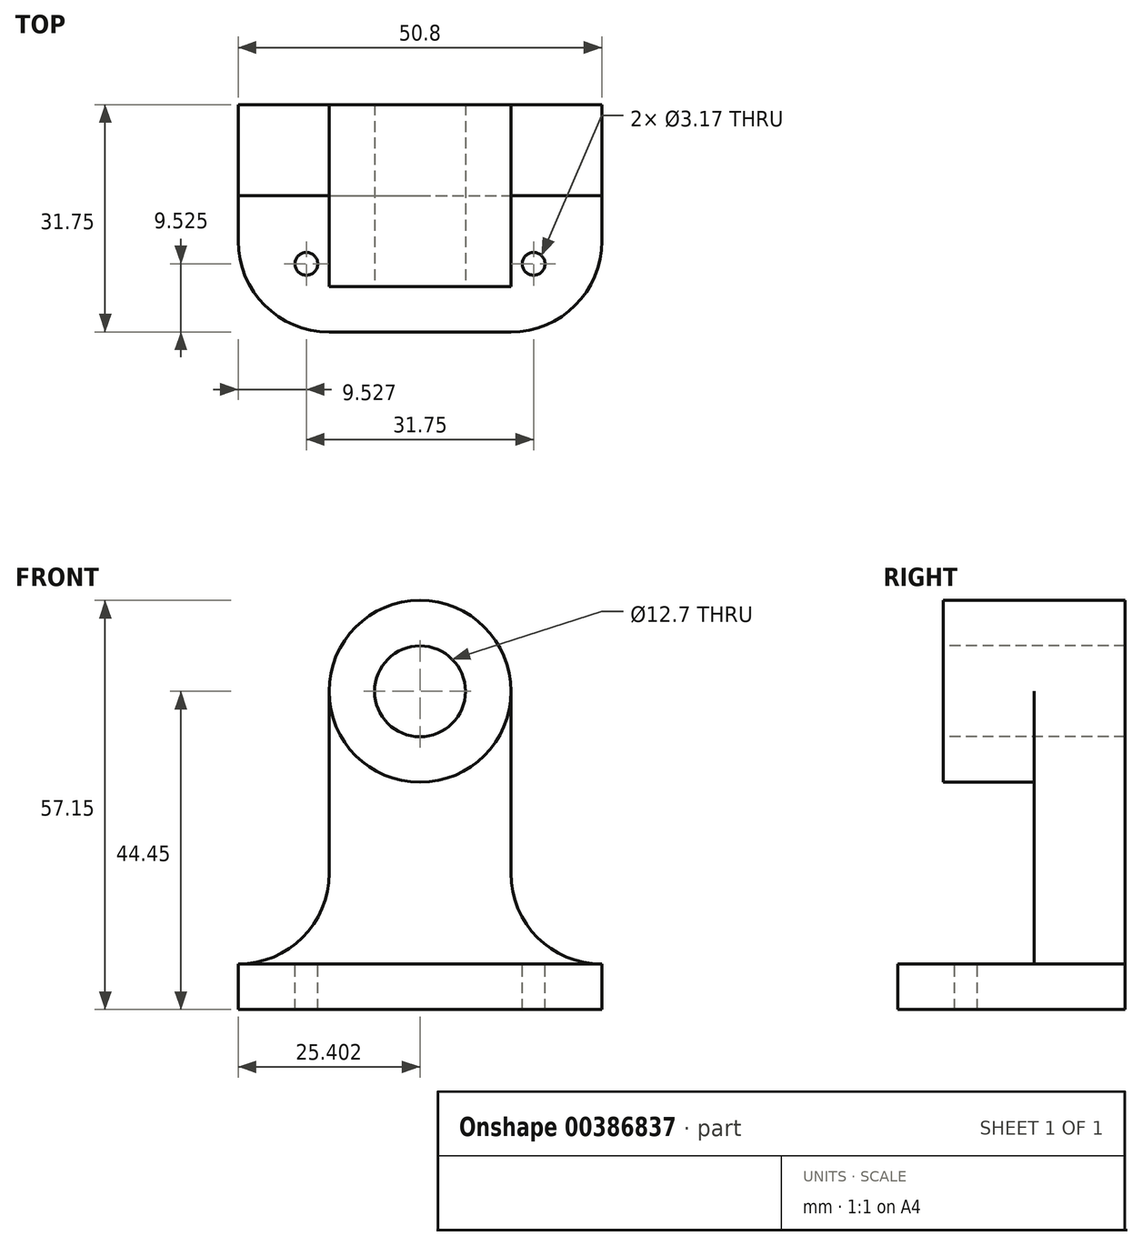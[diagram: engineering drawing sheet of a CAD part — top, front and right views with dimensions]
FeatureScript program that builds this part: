
annotation { "Feature Type Name" : "Feature", "Feature Type Description" : "" }
export const myFeature = defineFeature(function(context is Context, id is Id, definition is map)
    precondition{}
    {
        {
            var Q0;
            Q0=qCreatedBy(makeId("Front.planeOp"),FACE);
            var sketch = newSketch(context, id + "F0", { "sketchPlane" : qUnion([Q0])});
            skLineSegment(sketch, "E0", {"start": v(-22.4, 6.35) * mm, "end": v(-22.4, 0) * mm});
            skLineSegment(sketch, "E1", {"start": v(-22.4, 0) * mm, "end": v(28.4, 0) * mm});
            skLineSegment(sketch, "E2", {"start": v(28.4, 0) * mm, "end": v(28.4, 6.35) * mm});
            skLineSegment(sketch, "E3", {"start": v(28.4, 6.35) * mm, "end": v(15.7, 6.35) * mm});
            skLineSegment(sketch, "E4", {"start": v(-22.4, 6.35) * mm, "end": v(-9.7, 6.35) * mm});
            skLineSegment(sketch, "E5", {"start": v(-9.7, 6.35) * mm, "end": v(-9.7, 57.15) * mm});
            skLineSegment(sketch, "E6", {"start": v(15.7, 6.35) * mm, "end": v(15.7, 57.15) * mm});
            skLineSegment(sketch, "E7", {"start": v(15.7, 57.15) * mm, "end": v(-9.7, 57.15) * mm});
            skSolve(sketch);
        }
        {
            var Q0;
            Q0=makeQuery(id+"F0.imprint","IMPRINT",FACE,{"disambiguationData":[TD([[makeQuery(id+"F0.imprint","IMPRINT",EDGE,{"derivedFrom":sQuery(id+"F0.wireOp",EDGE,"E0")}),1.0]])]});
            extrude(context, id + "F1", {"entities" : qUnion([Q0]), "depth" : 31.75 * mm});
        }
        {
            var Q0;
            Q0=makeQuery(id+"F1.opExtrude","CAP_FACE",FACE,{"disambiguationData":[OSD([sQuery(id+"F0.wireOp",EDGE,"E0"),sQuery(id+"F0.wireOp",EDGE,"E1"),sQuery(id+"F0.wireOp",EDGE,"E2"),sQuery(id+"F0.wireOp",EDGE,"E3"),sQuery(id+"F0.wireOp",EDGE,"E4"),sQuery(id+"F0.wireOp",EDGE,"E5"),sQuery(id+"F0.wireOp",EDGE,"E6"),sQuery(id+"F0.wireOp",EDGE,"E7")])],"isStart":false});
            var sketch = newSketch(context, id + "F2", { "sketchPlane" : qUnion([Q0])});
            skCircle(sketch, "E8", {"center": v(3, 44.45) * mm, "radius": 6.35 * mm});
            skSolve(sketch);
        }
        {
            var Q0;
            Q0=makeQuery(id+"F2.imprint","IMPRINT",FACE,{"disambiguationData":[TD([[makeQuery(id+"F2.imprint","IMPRINT",EDGE,{"derivedFrom":sQuery(id+"F2.wireOp",EDGE,"E8")}),1.0]])]});
            extrude(context, id + "F3", {"entities" : qUnion([Q0]), "operationType" : NewBodyOperationType.REMOVE, "oppositeDirection" : true, "depth" : 31.75 * mm});
        }
        {
            var Q0;
            Q0=makeQuery(id+"F1.opExtrude","CAP_FACE",FACE,{"disambiguationData":[OSD([sQuery(id+"F0.wireOp",EDGE,"E0"),sQuery(id+"F0.wireOp",EDGE,"E1"),sQuery(id+"F0.wireOp",EDGE,"E2"),sQuery(id+"F0.wireOp",EDGE,"E3"),sQuery(id+"F0.wireOp",EDGE,"E4"),sQuery(id+"F0.wireOp",EDGE,"E5"),sQuery(id+"F0.wireOp",EDGE,"E6"),sQuery(id+"F0.wireOp",EDGE,"E7")])],"isStart":false});
            var sketch = newSketch(context, id + "F4", { "sketchPlane" : qUnion([Q0])});
            skCircle(sketch, "E9", {"center": v(3, 44.45) * mm, "radius": 12.7 * mm});
            skSolve(sketch);
        }
        {
            var Q0;
            {var subQ0=sQuery(id+"F4.wireOp",EDGE,"E9");var subQ1=makeQuery(id+"F1.opExtrude","CAP_EDGE",EDGE,{"disambiguationData":[OSD([sQuery(id+"F0.wireOp",EDGE,"E7")])],"isStart":false});var subQ2=makeQuery(id+"F4.imprint","INTERSECT",VERTEX,{"derivedFrom":[subQ1,subQ0]});Q0=makeQuery(id+"F4.imprint","IMPRINT",FACE,{"disambiguationData":[TD([[makeQuery(id+"F4.imprint","IMPRINT",EDGE,{"disambiguationData":[TD([[subQ2,-1.0]])],"derivedFrom":subQ0}),-1.0]])]});}
            var Q1;
            {var subQ0=sQuery(id+"F4.wireOp",EDGE,"E9");var subQ1=makeQuery(id+"F1.opExtrude","CAP_EDGE",EDGE,{"disambiguationData":[OSD([sQuery(id+"F0.wireOp",EDGE,"E7")])],"isStart":false});var subQ2=makeQuery(id+"F4.imprint","INTERSECT",VERTEX,{"derivedFrom":[subQ1,subQ0]});Q1=makeQuery(id+"F4.imprint","IMPRINT",FACE,{"disambiguationData":[TD([[makeQuery(id+"F4.imprint","IMPRINT",EDGE,{"disambiguationData":[TD([[subQ2,1.0]])],"derivedFrom":subQ0}),-1.0]])]});}
            extrude(context, id + "F5", {"entities" : qUnion([Q0, Q1]), "operationType" : NewBodyOperationType.REMOVE, "oppositeDirection" : true, "depth" : 31.75 * mm});
        }
        {
            var Q0;
            Q0=makeQuery(id+"F1.opExtrude","CAP_FACE",FACE,{"disambiguationData":[OSD([sQuery(id+"F0.wireOp",EDGE,"E0"),sQuery(id+"F0.wireOp",EDGE,"E1"),sQuery(id+"F0.wireOp",EDGE,"E2"),sQuery(id+"F0.wireOp",EDGE,"E3"),sQuery(id+"F0.wireOp",EDGE,"E4"),sQuery(id+"F0.wireOp",EDGE,"E5"),sQuery(id+"F0.wireOp",EDGE,"E6"),sQuery(id+"F0.wireOp",EDGE,"E7")])],"isStart":false});
            var sketch = newSketch(context, id + "F6", { "sketchPlane" : qUnion([Q0])});
            skCircle(sketch, "E10", {"center": v(3, 44.45) * mm, "radius": 12.7 * mm});
            skLineSegment(sketch, "E11", {"start": v(-9.7, 6.35) * mm, "end": v(15.7, 6.35) * mm});
            skSolve(sketch);
        }
        {
            var Q0;
            Q0=makeQuery(id+"F6.imprint","IMPRINT",FACE,{"disambiguationData":[TD([[makeQuery(id+"F6.imprint","IMPRINT",EDGE,{"derivedFrom":sQuery(id+"F6.wireOp",EDGE,"E11")}),1.0]])]});
            extrude(context, id + "F7", {"entities" : qUnion([Q0]), "operationType" : NewBodyOperationType.REMOVE, "oppositeDirection" : true, "depth" : 19.05 * mm});
        }
        {
            var Q0;
            {var subQ1=sQuery(id+"F0.wireOp",EDGE,"E7");var subQ3=sQuery(id+"F0.wireOp",EDGE,"E5");var subQ4=sQuery(id+"F0.wireOp",EDGE,"E6");Q0=makeQuery(id+"F7.boolean.opBoolean","SPLIT",FACE,{"disambiguationData":[TD([makeQuery(id+"F3.boolean.opBoolean","COPY",FACE,{"derivedFrom":makeQuery(id+"F3.opExtrude","SWEPT_FACE",FACE,{"disambiguationData":[OSD([sQuery(id+"F2.wireOp",EDGE,"E8")])]})})])],"derivedFrom":makeQuery(id+"F1.opExtrude","CAP_FACE",FACE,{"disambiguationData":[OSD([sQuery(id+"F0.wireOp",EDGE,"E0"),sQuery(id+"F0.wireOp",EDGE,"E1"),sQuery(id+"F0.wireOp",EDGE,"E2"),sQuery(id+"F0.wireOp",EDGE,"E3"),sQuery(id+"F0.wireOp",EDGE,"E4"),subQ3,subQ4,subQ1])],"isStart":false})});}
            extrude(context, id + "F8", {"entities" : qUnion([Q0]), "operationType" : NewBodyOperationType.REMOVE, "oppositeDirection" : true, "depth" : 6.35 * mm});
        }
        {
            var Q0;
            {var subQ0=sQuery(id+"F0.wireOp",EDGE,"E2");var subQ1=sQuery(id+"F0.wireOp",EDGE,"E1");var subQ2=sQuery(id+"F0.wireOp",EDGE,"E3");var subQ3=sQuery(id+"F0.wireOp",EDGE,"E0");var subQ4=sQuery(id+"F0.wireOp",EDGE,"E4");Q0=makeQuery(id+"F7.boolean.opBoolean","SPLIT",FACE,{"disambiguationData":[TD([makeQuery(id+"F1.opExtrude","SWEPT_FACE",FACE,{"disambiguationData":[OSD([subQ3])]})])],"derivedFrom":makeQuery(id+"F1.opExtrude","CAP_FACE",FACE,{"disambiguationData":[OSD([subQ3,subQ1,subQ0,subQ2,subQ4,sQuery(id+"F0.wireOp",EDGE,"E5"),sQuery(id+"F0.wireOp",EDGE,"E6"),sQuery(id+"F0.wireOp",EDGE,"E7")])],"isStart":false})});}
            var sketch = newSketch(context, id + "F9", { "sketchPlane" : qUnion([Q0])});
            skLineSegment(sketch, "E12", {"start": v(-22.4, 6.35) * mm, "end": v(-22.4, 19.05) * mm});
            skLineSegment(sketch, "E13", {"start": v(-22.4, 19.05) * mm, "end": v(-9.7, 19.05) * mm});
            skLineSegment(sketch, "E14", {"start": v(-9.7, 19.05) * mm, "end": v(-9.7, 6.35) * mm});
            skLineSegment(sketch, "E15", {"start": v(-9.7, 6.35) * mm, "end": v(-22.4, 6.35) * mm});
            skSolve(sketch);
        }
        {
            var Q0;
            Q0=makeQuery(id+"F9.imprint","IMPRINT",FACE,{"disambiguationData":[TD([[makeQuery(id+"F9.imprint","IMPRINT",EDGE,{"derivedFrom":sQuery(id+"F9.wireOp",EDGE,"E12")}),-1.0]])]});
            extrude(context, id + "F10", {"entities" : qUnion([Q0]), "operationType" : NewBodyOperationType.ADD, "oppositeDirection" : true, "depth" : 31.75 * mm});
        }
        {
            var Q0;
            {var subQ0=sQuery(id+"F0.wireOp",EDGE,"E2");var subQ1=sQuery(id+"F0.wireOp",EDGE,"E1");var subQ2=sQuery(id+"F0.wireOp",EDGE,"E3");var subQ3=sQuery(id+"F0.wireOp",EDGE,"E0");var subQ4=sQuery(id+"F0.wireOp",EDGE,"E4");Q0=makeQuery(id+"F10.boolean.opBoolean","MERGE",FACE,{"derivedFrom":[makeQuery(id+"F7.boolean.opBoolean","SPLIT",FACE,{"disambiguationData":[TD([makeQuery(id+"F1.opExtrude","SWEPT_FACE",FACE,{"disambiguationData":[OSD([subQ3])]})])],"derivedFrom":makeQuery(id+"F1.opExtrude","CAP_FACE",FACE,{"disambiguationData":[OSD([subQ3,subQ1,subQ0,subQ2,subQ4,sQuery(id+"F0.wireOp",EDGE,"E5"),sQuery(id+"F0.wireOp",EDGE,"E6"),sQuery(id+"F0.wireOp",EDGE,"E7")])],"isStart":false})}),makeQuery(id+"F10.opExtrude","CAP_FACE",FACE,{"disambiguationData":[OSD([sQuery(id+"F9.wireOp",EDGE,"E12"),sQuery(id+"F9.wireOp",EDGE,"E13"),sQuery(id+"F9.wireOp",EDGE,"E14"),sQuery(id+"F9.wireOp",EDGE,"E15")])],"isStart":true})]});}
            var sketch = newSketch(context, id + "F11", { "sketchPlane" : qUnion([Q0])});
            skLineSegment(sketch, "E16", {"start": v(-9.7, 6.35) * mm, "end": v(-22.4, 6.35) * mm});
            skLineSegment(sketch, "E17", {"start": v(-22.4, 6.35) * mm, "end": v(-22.4, 19.05) * mm});
            skLineSegment(sketch, "E18", {"start": v(-22.4, 19.05) * mm, "end": v(-9.7, 19.05) * mm});
            skLineSegment(sketch, "E19", {"start": v(-9.7, 19.05) * mm, "end": v(-9.7, 6.35) * mm});
            skSolve(sketch);
        }
        {
            var Q0;
            Q0=makeQuery(id+"F11.imprint","IMPRINT",FACE,{"disambiguationData":[TD([[makeQuery(id+"F11.imprint","IMPRINT",EDGE,{"derivedFrom":sQuery(id+"F11.wireOp",EDGE,"E16")}),-1.0]])]});
            extrude(context, id + "F12", {"entities" : qUnion([Q0]), "operationType" : NewBodyOperationType.REMOVE, "oppositeDirection" : true, "depth" : 19.05 * mm});
        }
        {
            var Q0;
            Q0=makeQuery(id+"F12.boolean.opBoolean","MERGE",FACE,{"derivedFrom":[makeQuery(id+"F7.boolean.opBoolean","COPY",FACE,{"derivedFrom":makeQuery(id+"F7.opExtrude","CAP_FACE",FACE,{"disambiguationData":[OSD([sQuery(id+"F0.wireOp",EDGE,"E5"),sQuery(id+"F0.wireOp",EDGE,"E6"),sQuery(id+"F6.wireOp",EDGE,"E10"),sQuery(id+"F6.wireOp",EDGE,"E11")])],"isStart":false})}),makeQuery(id+"F12.opExtrude","CAP_FACE",FACE,{"disambiguationData":[OSD([sQuery(id+"F11.wireOp",EDGE,"E16"),sQuery(id+"F11.wireOp",EDGE,"E17"),sQuery(id+"F11.wireOp",EDGE,"E18"),sQuery(id+"F11.wireOp",EDGE,"E19")])],"isStart":false})]});
            var sketch = newSketch(context, id + "F13", { "sketchPlane" : qUnion([Q0])});
            skArc(sketch, "E20", {"start": v(-22.4, 6.35) * mm, "mid": v(-13.42, 10.07) * mm, "end": v(-9.7, 19.05) * mm});
            skSolve(sketch);
        }
        {
            var Q0;
            Q0=makeQuery(id+"F13.imprint","IMPRINT",FACE,{"disambiguationData":[TD([[makeQuery(id+"F13.imprint","IMPRINT",EDGE,{"derivedFrom":sQuery(id+"F13.wireOp",EDGE,"E20")}),1.0]])]});
            extrude(context, id + "F14", {"entities" : qUnion([Q0]), "operationType" : NewBodyOperationType.REMOVE, "oppositeDirection" : true, "depth" : 12.7 * mm});
        }
        {
            var Q0;
            Q0=makeQuery(id+"F12.boolean.opBoolean","MERGE",FACE,{"derivedFrom":[makeQuery(id+"F7.boolean.opBoolean","COPY",FACE,{"derivedFrom":makeQuery(id+"F7.opExtrude","CAP_FACE",FACE,{"disambiguationData":[OSD([sQuery(id+"F0.wireOp",EDGE,"E5"),sQuery(id+"F0.wireOp",EDGE,"E6"),sQuery(id+"F6.wireOp",EDGE,"E10"),sQuery(id+"F6.wireOp",EDGE,"E11")])],"isStart":false})}),makeQuery(id+"F12.opExtrude","CAP_FACE",FACE,{"disambiguationData":[OSD([sQuery(id+"F11.wireOp",EDGE,"E16"),sQuery(id+"F11.wireOp",EDGE,"E17"),sQuery(id+"F11.wireOp",EDGE,"E18"),sQuery(id+"F11.wireOp",EDGE,"E19")])],"isStart":false})]});
            var sketch = newSketch(context, id + "F15", { "sketchPlane" : qUnion([Q0])});
            skLineSegment(sketch, "E21", {"start": v(15.7, 6.35) * mm, "end": v(15.7, 19.05) * mm});
            skLineSegment(sketch, "E22", {"start": v(15.7, 6.35) * mm, "end": v(28.4, 6.35) * mm});
            skLineSegment(sketch, "E23", {"start": v(28.4, 6.35) * mm, "end": v(28.4, 19.05) * mm});
            skLineSegment(sketch, "E24", {"start": v(28.4, 19.05) * mm, "end": v(15.7, 19.05) * mm});
            skSolve(sketch);
        }
        {
            var Q0;
            Q0=makeQuery(id+"F15.imprint","IMPRINT",FACE,{"disambiguationData":[TD([[makeQuery(id+"F15.imprint","IMPRINT",EDGE,{"derivedFrom":sQuery(id+"F15.wireOp",EDGE,"E21")}),-1.0]])]});
            extrude(context, id + "F16", {"entities" : qUnion([Q0]), "operationType" : NewBodyOperationType.ADD, "oppositeDirection" : true, "depth" : 12.7 * mm});
        }
        {
            var Q0;
            Q0=makeQuery(id+"F16.boolean.opBoolean","MERGE",FACE,{"derivedFrom":[makeQuery(id+"F12.boolean.opBoolean","MERGE",FACE,{"derivedFrom":[makeQuery(id+"F7.boolean.opBoolean","COPY",FACE,{"derivedFrom":makeQuery(id+"F7.opExtrude","CAP_FACE",FACE,{"disambiguationData":[OSD([sQuery(id+"F0.wireOp",EDGE,"E5"),sQuery(id+"F0.wireOp",EDGE,"E6"),sQuery(id+"F6.wireOp",EDGE,"E10"),sQuery(id+"F6.wireOp",EDGE,"E11")])],"isStart":false})}),makeQuery(id+"F12.opExtrude","CAP_FACE",FACE,{"disambiguationData":[OSD([sQuery(id+"F11.wireOp",EDGE,"E16"),sQuery(id+"F11.wireOp",EDGE,"E17"),sQuery(id+"F11.wireOp",EDGE,"E18"),sQuery(id+"F11.wireOp",EDGE,"E19")])],"isStart":false})]}),makeQuery(id+"F16.opExtrude","CAP_FACE",FACE,{"disambiguationData":[OSD([sQuery(id+"F15.wireOp",EDGE,"E21"),sQuery(id+"F15.wireOp",EDGE,"E22"),sQuery(id+"F15.wireOp",EDGE,"E23"),sQuery(id+"F15.wireOp",EDGE,"E24")])],"isStart":true})]});
            var sketch = newSketch(context, id + "F17", { "sketchPlane" : qUnion([Q0])});
            skArc(sketch, "E25", {"start": v(15.7, 19.05) * mm, "mid": v(19.42, 10.07) * mm, "end": v(28.4, 6.35) * mm});
            skSolve(sketch);
        }
        {
            var Q0;
            Q0=makeQuery(id+"F17.imprint","IMPRINT",FACE,{"disambiguationData":[TD([[makeQuery(id+"F17.imprint","IMPRINT",EDGE,{"derivedFrom":sQuery(id+"F17.wireOp",EDGE,"E25")}),1.0]])]});
            extrude(context, id + "F18", {"entities" : qUnion([Q0]), "operationType" : NewBodyOperationType.REMOVE, "oppositeDirection" : true, "depth" : 12.7 * mm});
        }
        {
            var Q0;
            Q0=makeQuery(id+"F12.boolean.opBoolean","MERGE",FACE,{"derivedFrom":[makeQuery(id+"F7.boolean.opBoolean","MERGE",FACE,{"derivedFrom":[makeQuery(id+"F1.opExtrude","SWEPT_FACE",FACE,{"disambiguationData":[OSD([sQuery(id+"F0.wireOp",EDGE,"E3")])]}),makeQuery(id+"F1.opExtrude","SWEPT_FACE",FACE,{"disambiguationData":[OSD([sQuery(id+"F0.wireOp",EDGE,"E4")])]}),makeQuery(id+"F7.opExtrude","SWEPT_FACE",FACE,{"disambiguationData":[OSD([sQuery(id+"F6.wireOp",EDGE,"E11")])]})]}),makeQuery(id+"F12.opExtrude","SWEPT_FACE",FACE,{"disambiguationData":[OSD([sQuery(id+"F11.wireOp",EDGE,"E16")])]})]});
            var sketch = newSketch(context, id + "F19", { "sketchPlane" : qUnion([Q0])});
            skCircle(sketch, "E26", {"center": v(-12.87, -22.23) * mm, "radius": 1.59 * mm});
            skCircle(sketch, "E27", {"center": v(18.88, -22.23) * mm, "radius": 1.59 * mm});
            skSolve(sketch);
        }
        {
            var Q0;
            Q0=makeQuery(id+"F19.imprint","IMPRINT",FACE,{"disambiguationData":[TD([[makeQuery(id+"F19.imprint","IMPRINT",EDGE,{"derivedFrom":sQuery(id+"F19.wireOp",EDGE,"E26")}),1.0]])]});
            var Q1;
            Q1=makeQuery(id+"F19.imprint","IMPRINT",FACE,{"disambiguationData":[TD([[makeQuery(id+"F19.imprint","IMPRINT",EDGE,{"derivedFrom":sQuery(id+"F19.wireOp",EDGE,"E27")}),1.0]])]});
            extrude(context, id + "F20", {"entities" : qUnion([Q0, Q1]), "operationType" : NewBodyOperationType.REMOVE, "oppositeDirection" : true, "depth" : 12.7 * mm});
        }
        {
            var Q0;
            Q0=makeQuery(id+"F12.boolean.opBoolean","MERGE",FACE,{"derivedFrom":[makeQuery(id+"F7.boolean.opBoolean","MERGE",FACE,{"derivedFrom":[makeQuery(id+"F1.opExtrude","SWEPT_FACE",FACE,{"disambiguationData":[OSD([sQuery(id+"F0.wireOp",EDGE,"E3")])]}),makeQuery(id+"F1.opExtrude","SWEPT_FACE",FACE,{"disambiguationData":[OSD([sQuery(id+"F0.wireOp",EDGE,"E4")])]}),makeQuery(id+"F7.opExtrude","SWEPT_FACE",FACE,{"disambiguationData":[OSD([sQuery(id+"F6.wireOp",EDGE,"E11")])]})]}),makeQuery(id+"F12.opExtrude","SWEPT_FACE",FACE,{"disambiguationData":[OSD([sQuery(id+"F11.wireOp",EDGE,"E16")])]})]});
            var sketch = newSketch(context, id + "F21", { "sketchPlane" : qUnion([Q0])});
            skArc(sketch, "E28", {"start": v(-22.4, -19.05) * mm, "mid": v(-18.68, -28.03) * mm, "end": v(-9.7, -31.75) * mm});
            skArc(sketch, "E29", {"start": v(15.7, -31.75) * mm, "mid": v(24.68, -28.03) * mm, "end": v(28.4, -19.05) * mm});
            skSolve(sketch);
        }
        {
            var Q0;
            {var subQ0=sQuery(id+"F21.wireOp",EDGE,"E28");Q0=makeQuery(id+"F21.imprint","IMPRINT",FACE,{"disambiguationData":[TD([[makeQuery(id+"F21.imprint","IMPRINT",EDGE,{"derivedFrom":subQ0}),-1.0]])]});}
            var Q1;
            {var subQ0=sQuery(id+"F21.wireOp",EDGE,"E29");Q1=makeQuery(id+"F21.imprint","IMPRINT",FACE,{"disambiguationData":[TD([[makeQuery(id+"F21.imprint","IMPRINT",EDGE,{"derivedFrom":subQ0}),-1.0]])]});}
            extrude(context, id + "F22", {"entities" : qUnion([Q0, Q1]), "operationType" : NewBodyOperationType.REMOVE, "oppositeDirection" : true, "depth" : 6.35 * mm});
        }
    });
